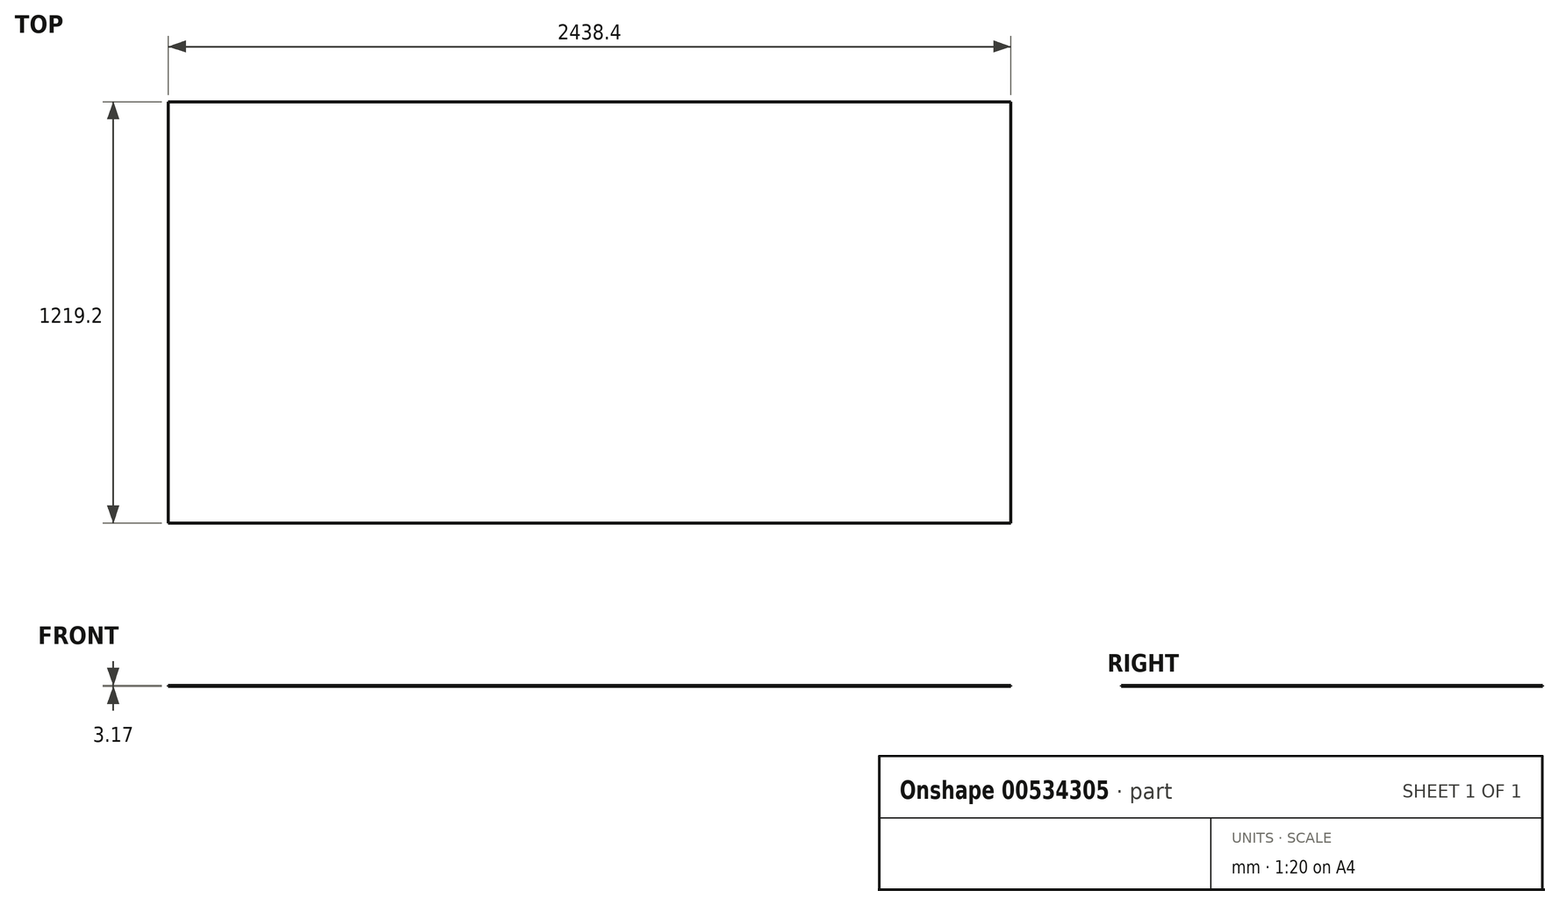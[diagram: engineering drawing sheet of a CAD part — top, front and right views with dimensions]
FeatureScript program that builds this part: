
annotation { "Feature Type Name" : "Feature", "Feature Type Description" : "" }
export const myFeature = defineFeature(function(context is Context, id is Id, definition is map)
    precondition{}
    {
        {
            var Q0;
            Q0=qCreatedBy(makeId("Top.planeOp"),FACE);
            var sketch = newSketch(context, id + "F0", { "sketchPlane" : qUnion([Q0])});
            skLineSegment(sketch, "E0.bottom", {"start": v(1219.2, -609.6) * mm, "end": v(-1219.2, -609.6) * mm});
            skLineSegment(sketch, "E0.top", {"start": v(1219.2, 609.6) * mm, "end": v(-1219.2, 609.6) * mm});
            skLineSegment(sketch, "E0.left", {"start": v(1219.2, -609.6) * mm, "end": v(1219.2, 609.6) * mm});
            skLineSegment(sketch, "E0.right", {"start": v(-1219.2, -609.6) * mm, "end": v(-1219.2, 609.6) * mm});
            skPoint(sketch, "E0.middle", {"position": v(0, 0) * mm});
            skSolve(sketch);
        }
        {
            var Q0;
            Q0=qSketchRegion(id+"F0",true);
            extrude(context, id + "F1", {"entities" : qUnion([Q0]), "depth" : 3.17 * mm, "offsetDistance" : 25.4 * mm});
        }
    });
